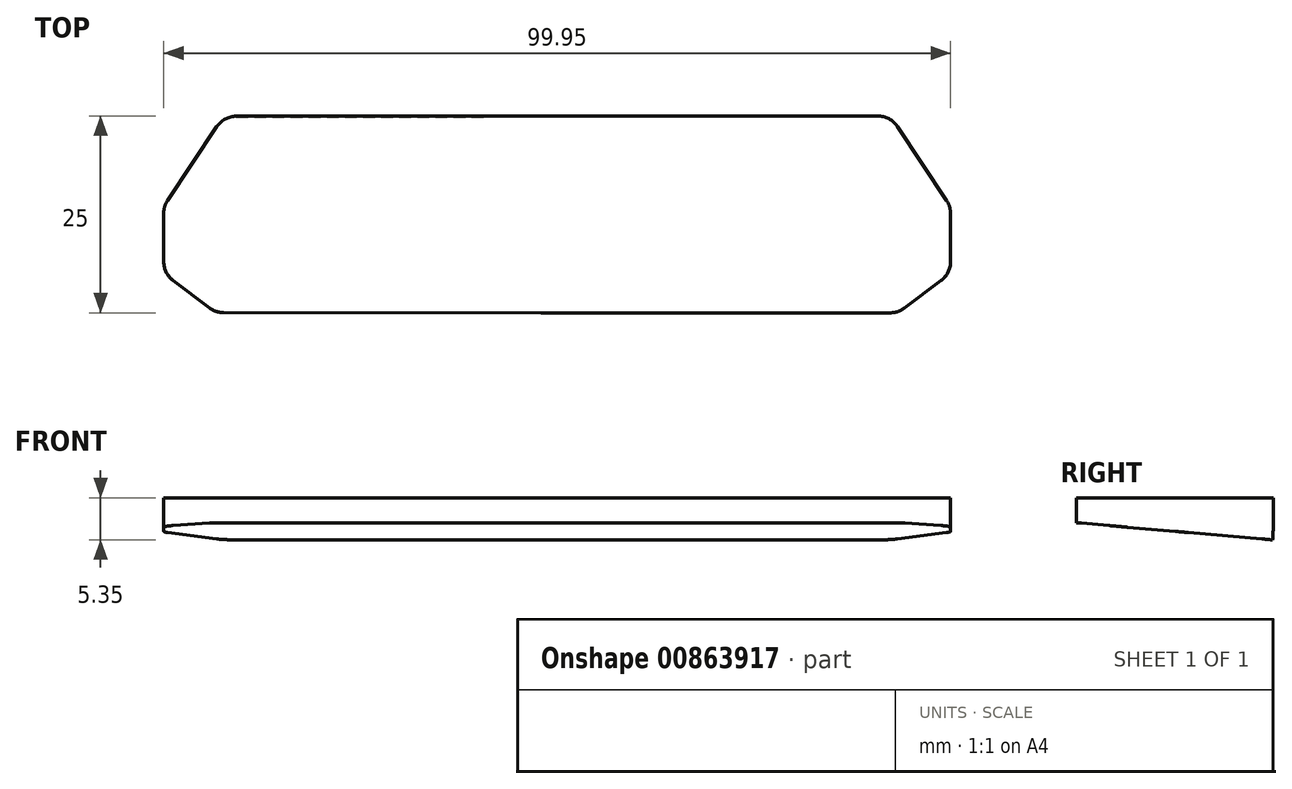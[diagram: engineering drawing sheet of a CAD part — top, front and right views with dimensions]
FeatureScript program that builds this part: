
annotation { "Feature Type Name" : "Feature", "Feature Type Description" : "" }
export const myFeature = defineFeature(function(context is Context, id is Id, definition is map)
    precondition{}
    {
        {
            var Q0;
            Q0=qCreatedBy(makeId("Top.planeOp"),FACE);
            var sketch = newSketch(context, id + "F0", { "sketchPlane" : qUnion([Q0])});
            skLineSegment(sketch, "E0.0", {"start": v(-42.35, 12.46) * mm, "end": v(0, 12.5) * mm});
            skLineSegment(sketch, "E0.1", {"start": v(42.32, 12.5) * mm, "end": v(0, 12.5) * mm});
            skLineSegment(sketch, "E0.2", {"start": v(-42.35, 12.46) * mm, "end": v(-49.97, 1.03) * mm});
            skLineSegment(sketch, "E0.3", {"start": v(42.32, 12.5) * mm, "end": v(49.98, 1) * mm});
            skLineSegment(sketch, "E0.4", {"start": v(49.98, 1) * mm, "end": v(49.98, -7.48) * mm});
            skLineSegment(sketch, "E0.5", {"start": v(49.98, -7.48) * mm, "end": v(43.33, -12.5) * mm});
            skLineSegment(sketch, "E0.6", {"start": v(-49.97, 1.03) * mm, "end": v(-49.95, -7.5) * mm});
            skLineSegment(sketch, "E0.7", {"start": v(-49.95, -7.5) * mm, "end": v(-43.35, -12.48) * mm});
            skLineSegment(sketch, "E0.8", {"start": v(-43.35, -12.48) * mm, "end": v(0, -12.5) * mm});
            skLineSegment(sketch, "E0.9", {"start": v(43.33, -12.5) * mm, "end": v(0, -12.5) * mm});
            skSolve(sketch);
        }
        {
            var Q0;
            Q0 = qSketchRegion(id + "F0", true);
            extrude(context, id + "F1", {"entities" : qUnion([Q0]), "depth" : 3.17 * mm, "offsetDistance" : 25.4 * mm});
        }
        {
            var Q0;
            Q0=qCreatedBy(makeId("Top.planeOp"),FACE);
            var sketch = newSketch(context, id + "F2", { "sketchPlane" : qUnion([Q0])});
            skLineSegment(sketch, "E1.0", {"start": v(-42.35, 12.46) * mm, "end": v(0, 12.5) * mm});
            skLineSegment(sketch, "E1.1", {"start": v(42.32, 12.5) * mm, "end": v(0, 12.5) * mm});
            skLineSegment(sketch, "E1.2", {"start": v(-42.35, 12.46) * mm, "end": v(-49.97, 1.03) * mm});
            skLineSegment(sketch, "E1.3", {"start": v(42.32, 12.5) * mm, "end": v(49.98, 1) * mm});
            skLineSegment(sketch, "E1.4", {"start": v(49.98, 1) * mm, "end": v(49.98, -7.48) * mm});
            skLineSegment(sketch, "E1.5", {"start": v(49.98, -7.48) * mm, "end": v(43.33, -12.5) * mm});
            skLineSegment(sketch, "E1.6", {"start": v(-49.97, 1.03) * mm, "end": v(-49.95, -7.5) * mm});
            skLineSegment(sketch, "E1.7", {"start": v(-49.95, -7.5) * mm, "end": v(-43.35, -12.48) * mm});
            skLineSegment(sketch, "E1.8", {"start": v(-43.35, -12.48) * mm, "end": v(0, -12.5) * mm});
            skLineSegment(sketch, "E1.9", {"start": v(43.33, -12.5) * mm, "end": v(0, -12.5) * mm});
            skSolve(sketch);
        }
        {
            var Q0;
            Q0 = qSketchRegion(id + "F2", true);
            var Q1;
            Q1=sQuery(id+"F2.wireOp",EDGE,"E1.9");
            revolve(context, id + "F3", {"operationType" : NewBodyOperationType.ADD, "surfaceOperationType" : NewSurfaceOperationType.NEW, "entities" : qUnion([Q0]), "axis" : qUnion([Q1]), "revolveType" : RevolveType.ONE_DIRECTION, "angle" : 5 * degree});
        }
        {
            var Q0;
            Q0=makeQuery(id+"F1.opExtrude","SWEPT_EDGE",EDGE,{"disambiguationData":[OSD([sQuery(id+"F0.wireOp",EDGE,"E0.1"),sQuery(id+"F0.wireOp",EDGE,"E0.3")])]});
            var Q1;
            Q1=makeQuery(id+"F1.opExtrude","SWEPT_EDGE",EDGE,{"disambiguationData":[OSD([sQuery(id+"F0.wireOp",EDGE,"E0.3"),sQuery(id+"F0.wireOp",EDGE,"E0.4")])]});
            var Q2;
            Q2=makeQuery(id+"F1.opExtrude","SWEPT_EDGE",EDGE,{"disambiguationData":[OSD([sQuery(id+"F0.wireOp",EDGE,"E0.4"),sQuery(id+"F0.wireOp",EDGE,"E0.5")])]});
            var Q3;
            Q3=makeQuery(id+"F1.opExtrude","SWEPT_EDGE",EDGE,{"disambiguationData":[OSD([sQuery(id+"F0.wireOp",EDGE,"E0.5"),sQuery(id+"F0.wireOp",EDGE,"E0.9")])]});
            var Q4;
            Q4=makeQuery(id+"F1.opExtrude","SWEPT_EDGE",EDGE,{"disambiguationData":[OSD([sQuery(id+"F0.wireOp",EDGE,"E0.0"),sQuery(id+"F0.wireOp",EDGE,"E0.2")])]});
            var Q5;
            Q5=makeQuery(id+"F1.opExtrude","SWEPT_EDGE",EDGE,{"disambiguationData":[OSD([sQuery(id+"F0.wireOp",EDGE,"E0.2"),sQuery(id+"F0.wireOp",EDGE,"E0.6")])]});
            var Q6;
            Q6=makeQuery(id+"F1.opExtrude","SWEPT_EDGE",EDGE,{"disambiguationData":[OSD([sQuery(id+"F0.wireOp",EDGE,"E0.6"),sQuery(id+"F0.wireOp",EDGE,"E0.7")])]});
            var Q7;
            Q7=makeQuery(id+"F1.opExtrude","SWEPT_EDGE",EDGE,{"disambiguationData":[OSD([sQuery(id+"F0.wireOp",EDGE,"E0.7"),sQuery(id+"F0.wireOp",EDGE,"E0.8")])]});
            fillet(context, id + "F4", {"entities" : qUnion([Q0, Q1, Q2, Q3, Q4, Q5, Q6, Q7]), "radius" : 3 * mm, "tangentPropagation" : true, "allowEdgeOverflow" : false});
        }
    });
